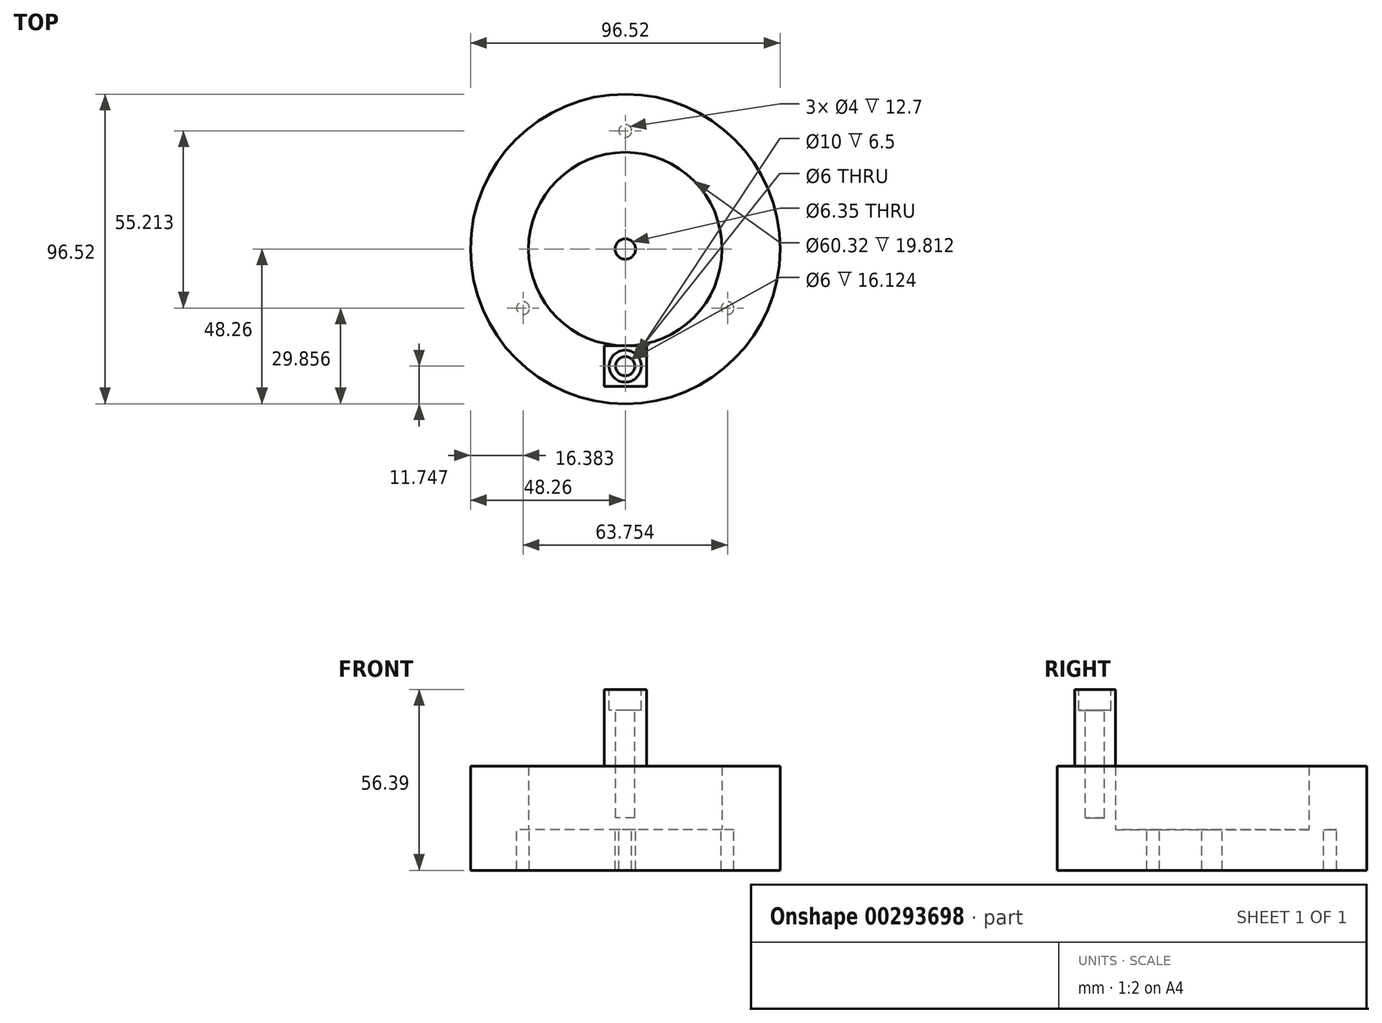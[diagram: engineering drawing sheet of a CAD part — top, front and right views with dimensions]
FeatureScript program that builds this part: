
annotation { "Feature Type Name" : "Feature", "Feature Type Description" : "" }
export const myFeature = defineFeature(function(context is Context, id is Id, definition is map)
    precondition{}
    {
        {
            var Q0;
            Q0=qCreatedBy(makeId("Top.planeOp"),FACE);
            var sketch = newSketch(context, id + "F0", { "sketchPlane" : qUnion([Q0])});
            skCircle(sketch, "E0", {"center": v(0, 0) * mm, "radius": 30.16 * mm});
            skCircle(sketch, "E1", {"center": v(0, 0) * mm, "radius": 48.26 * mm});
            skCircle(sketch, "E2", {"center": v(0, 36.8) * mm, "radius": 2 * mm});
            skCircle(sketch, "E3", {"center": v(0, 0) * mm, "radius": 36.8 * mm, "construction": true});
            skCircle(sketch, "E4.1.0", {"center": v(-31.88, -18.4) * mm, "radius": 2 * mm});
            skCircle(sketch, "E4.2.0", {"center": v(31.88, -18.4) * mm, "radius": 2 * mm});
            skCircle(sketch, "E5", {"center": v(0, 0) * mm, "radius": 3.18 * mm});
            skSolve(sketch);
        }
        {
            var Q0;
            Q0=makeQuery(id+"F0.imprint","IMPRINT",FACE,{"disambiguationData":[TD([[makeQuery(id+"F0.imprint","IMPRINT",EDGE,{"derivedFrom":sQuery(id+"F0.wireOp",EDGE,"E0")}),-1.0]])]});
            var Q1;
            Q1=makeQuery(id+"F0.imprint","IMPRINT",FACE,{"disambiguationData":[TD([[makeQuery(id+"F0.imprint","IMPRINT",EDGE,{"derivedFrom":sQuery(id+"F0.wireOp",EDGE,"E0")}),1.0]])]});
            extrude(context, id + "F1", {"entities" : qUnion([Q0, Q1]), "oppositeDirection" : true, "depth" : 12.7 * mm});
        }
        {
            var Q0;
            Q0=makeQuery(id+"F0.imprint","IMPRINT",FACE,{"disambiguationData":[TD([[makeQuery(id+"F0.imprint","IMPRINT",EDGE,{"derivedFrom":sQuery(id+"F0.wireOp",EDGE,"E0")}),-1.0]])]});
            var Q1;
            Q1=makeQuery(id+"F0.imprint","IMPRINT",FACE,{"disambiguationData":[TD([[makeQuery(id+"F0.imprint","IMPRINT",EDGE,{"derivedFrom":sQuery(id+"F0.wireOp",EDGE,"E2")}),1.0]])]});
            var Q2;
            Q2=makeQuery(id+"F0.imprint","IMPRINT",FACE,{"disambiguationData":[TD([[makeQuery(id+"F0.imprint","IMPRINT",EDGE,{"derivedFrom":sQuery(id+"F0.wireOp",EDGE,"E4.1.0")}),1.0]])]});
            var Q3;
            Q3=makeQuery(id+"F0.imprint","IMPRINT",FACE,{"disambiguationData":[TD([[makeQuery(id+"F0.imprint","IMPRINT",EDGE,{"derivedFrom":sQuery(id+"F0.wireOp",EDGE,"E4.2.0")}),1.0]])]});
            extrude(context, id + "F2", {"entities" : qUnion([Q0, Q1, Q2, Q3]), "operationType" : NewBodyOperationType.ADD, "depth" : 19.8 * mm});
        }
        {
            var Q0;
            Q0=makeQuery(id+"F2.opExtrude","CAP_FACE",FACE,{"disambiguationData":[OSD([sQuery(id+"F0.wireOp",EDGE,"E0"),sQuery(id+"F0.wireOp",EDGE,"E1")])],"isStart":false});
            var sketch = newSketch(context, id + "F3", { "sketchPlane" : qUnion([Q0])});
            skCircle(sketch, "E6.0", {"center": v(-31.88, -18.4) * mm, "radius": 2 * mm});
            skCircle(sketch, "E7.0", {"center": v(31.88, -18.4) * mm, "radius": 2 * mm});
            skLineSegment(sketch, "E8", {"start": v(-31.88, -18.4) * mm, "end": v(31.88, -18.4) * mm, "construction": true});
            skLineSegment(sketch, "E9", {"start": v(0, -18.4) * mm, "end": v(0, -63.54) * mm, "construction": true});
            skPoint(sketch, "E10", {"position": v(0, -36.51) * mm});
            skLineSegment(sketch, "E11.bottom", {"start": v(-6.6, -30.16) * mm, "end": v(6.6, -30.16) * mm});
            skLineSegment(sketch, "E11.top", {"start": v(-6.6, -42.86) * mm, "end": v(6.6, -42.86) * mm});
            skLineSegment(sketch, "E11.left", {"start": v(-6.6, -30.16) * mm, "end": v(-6.6, -42.86) * mm});
            skLineSegment(sketch, "E11.right", {"start": v(6.6, -30.16) * mm, "end": v(6.6, -42.86) * mm});
            skSolve(sketch);
        }
        {
            var Q0;
            Q0=makeQuery(id+"F3.imprint","IMPRINT",FACE,{"disambiguationData":[TD([[makeQuery(id+"F3.imprint","IMPRINT",EDGE,{"derivedFrom":sQuery(id+"F3.wireOp",EDGE,"E11.top")}),1.0]])]});
            extrude(context, id + "F4", {"entities" : qUnion([Q0]), "depth" : 23.88 * mm});
        }
        {
            var Q0;
            Q0=makeQuery(id+"F4.opExtrude","CAP_FACE",FACE,{"disambiguationData":[OSD([sQuery(id+"F3.wireOp",EDGE,"E11.bottom"),sQuery(id+"F3.wireOp",EDGE,"E11.top"),sQuery(id+"F3.wireOp",EDGE,"E11.left"),sQuery(id+"F3.wireOp",EDGE,"E11.right")])],"isStart":false});
            var sketch = newSketch(context, id + "F5", { "sketchPlane" : qUnion([Q0])});
            skLineSegment(sketch, "E12.0.0", {"start": v(-6.6, -30.16) * mm, "end": v(-6.6, -42.86) * mm});
            skLineSegment(sketch, "E12.0.1", {"start": v(-6.6, -42.86) * mm, "end": v(6.6, -42.86) * mm});
            skLineSegment(sketch, "E12.0.2", {"start": v(6.6, -42.86) * mm, "end": v(6.6, -30.16) * mm});
            skLineSegment(sketch, "E12.0.3", {"start": v(6.6, -30.16) * mm, "end": v(-6.6, -30.16) * mm});
            skLineSegment(sketch, "E13", {"start": v(6.6, -30.16) * mm, "end": v(-6.6, -42.86) * mm, "construction": true});
            skCircle(sketch, "E14", {"center": v(0, -36.51) * mm, "radius": 3 * mm});
            skCircle(sketch, "E15", {"center": v(0, -36.51) * mm, "radius": 5 * mm});
            skSolve(sketch);
        }
        {
            var Q0;
            Q0=makeQuery(id+"F5.imprint","IMPRINT",FACE,{"disambiguationData":[TD([[makeQuery(id+"F5.imprint","IMPRINT",EDGE,{"derivedFrom":sQuery(id+"F5.wireOp",EDGE,"E14")}),-1.0]])]});
            var Q1;
            Q1=makeQuery(id+"F5.imprint","IMPRINT",FACE,{"disambiguationData":[TD([[makeQuery(id+"F5.imprint","IMPRINT",EDGE,{"derivedFrom":sQuery(id+"F5.wireOp",EDGE,"E14")}),1.0]])]});
            extrude(context, id + "F6", {"entities" : qUnion([Q0, Q1]), "operationType" : NewBodyOperationType.REMOVE, "oppositeDirection" : true, "depth" : 6.5 * mm});
        }
        {
            var Q0;
            Q0=makeQuery(id+"F5.imprint","IMPRINT",FACE,{"disambiguationData":[TD([[makeQuery(id+"F5.imprint","IMPRINT",EDGE,{"derivedFrom":sQuery(id+"F5.wireOp",EDGE,"E14")}),1.0]])]});
            extrude(context, id + "F7", {"entities" : qUnion([Q0]), "operationType" : NewBodyOperationType.REMOVE, "oppositeDirection" : true, "depth" : 30 * mm + 10 * mm});
        }
    });
